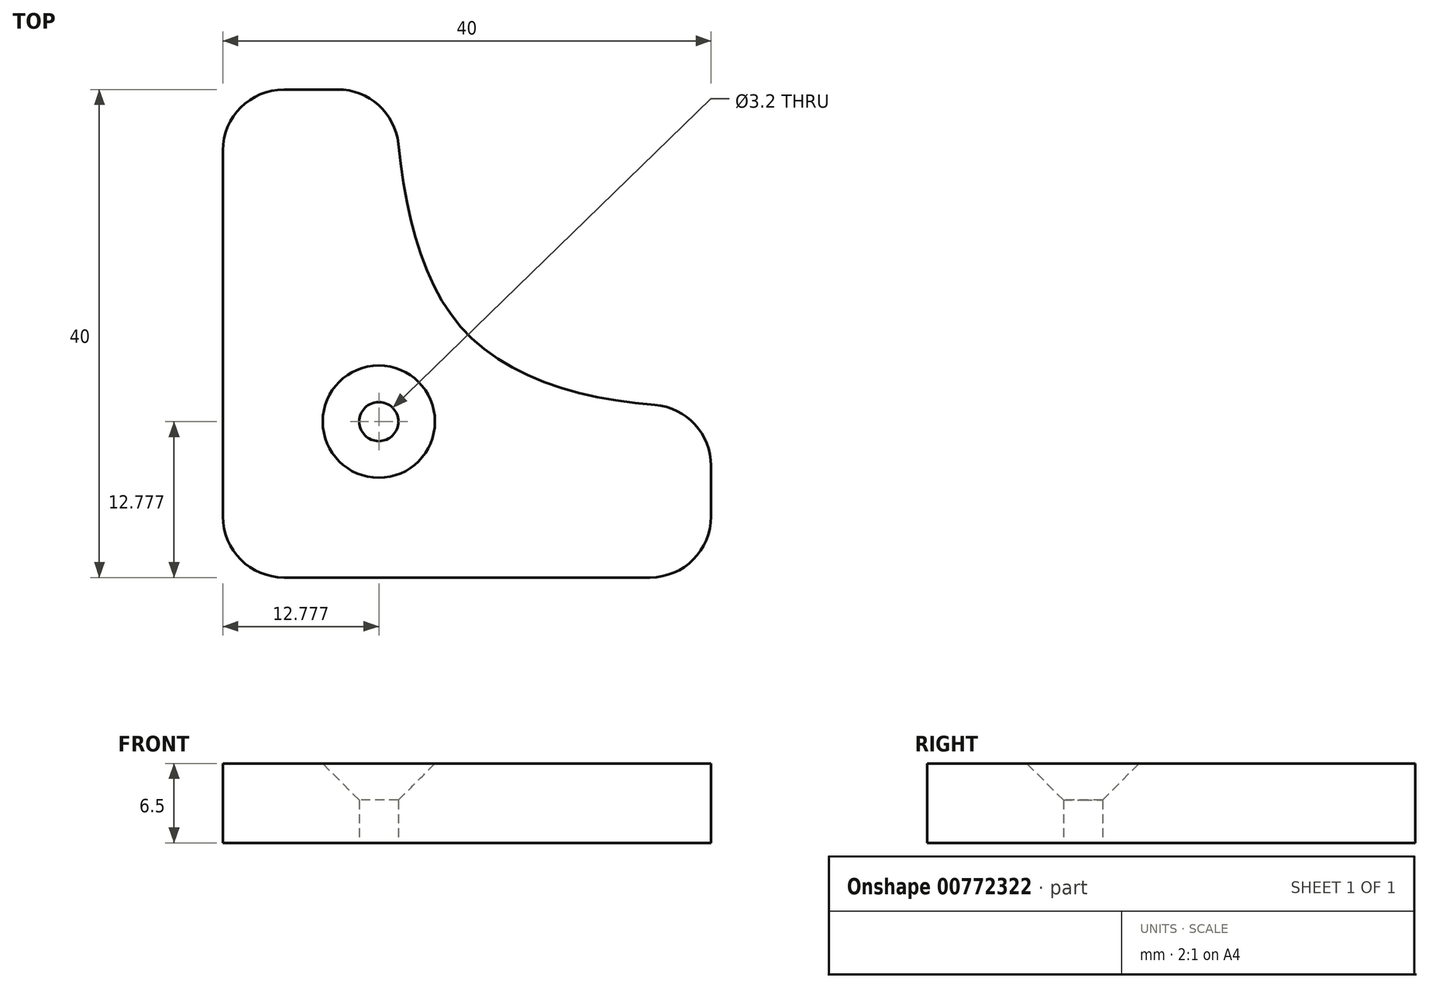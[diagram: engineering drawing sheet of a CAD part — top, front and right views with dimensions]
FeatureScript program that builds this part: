
annotation { "Feature Type Name" : "Feature", "Feature Type Description" : "" }
export const myFeature = defineFeature(function(context is Context, id is Id, definition is map)
    precondition{}
    {
        {
            assignVariable(context, id + "F0", {"name" : "h", "anyValue" : 6.5});
        }
        {
            var Q0;
            Q0=qCreatedBy(makeId("Top.planeOp"),FACE);
            var sketch = newSketch(context, id + "F1", { "sketchPlane" : qUnion([Q0])});
            skLineSegment(sketch, "E0.bottom", {"start": v(-20, 20) * mm, "end": v(20, 20) * mm});
            skLineSegment(sketch, "E0.top", {"start": v(-20, -20) * mm, "end": v(20, -20) * mm});
            skLineSegment(sketch, "E0.left", {"start": v(-20, 20) * mm, "end": v(-20, -20) * mm});
            skLineSegment(sketch, "E0.right", {"start": v(20, 20) * mm, "end": v(20, -20) * mm});
            skPoint(sketch, "E1", {"position": v(0, -20) * mm});
            skPoint(sketch, "E2", {"position": v(-20, 0) * mm});
            skFitSpline(sketch, "E3", {"points": [v(-6, 20) * mm, v(0, 0) * mm, v(20, -6) * mm], "startDerivative": vector(3.16, -47.96) * mm, "endDerivative": vector(47.54, 0.6) * mm});
            skLineSegment(sketch, "E4", {"start": v(-20, -20) * mm, "end": v(0, 0) * mm, "construction": true});
            skPoint(sketch, "E5", {"position": v(-7.22, -7.22) * mm});
            skCircle(sketch, "E6", {"center": v(-7.22, -7.22) * mm, "radius": 1.6 * mm});
            skSolve(sketch);
        }
        {
            var Q0;
            {var subQ1=sQuery(id+"F1.wireOp",EDGE,"E0.top");Q0=makeQuery(id+"F1.imprint","IMPRINT",FACE,{"disambiguationData":[TD([[makeQuery(id+"F1.imprint","IMPRINT",EDGE,{"derivedFrom":subQ1}),1.0]])]});}
            extrude(context, id + "F2", {"entities" : qUnion([Q0]), "depth" : (getVariable(context, 'h')) * mm, "offsetDistance" : 25 * mm});
        }
        {
            var Q0;
            Q0=makeQuery(id+"F2.opExtrude","CAP_EDGE",EDGE,{"disambiguationData":[OSD([sQuery(id+"F1.wireOp",EDGE,"E6")])],"isStart":false});
            chamfer(context, id + "F3", {"entities" : qUnion([Q0]), "width" : 3 * mm, "tangentPropagation" : true});
        }
        {
            var Q0;
            Q0=makeQuery(id+"F2.opExtrude","SWEPT_EDGE",EDGE,{"disambiguationData":[OSD([sQuery(id+"F1.wireOp",EDGE,"E0.top"),sQuery(id+"F1.wireOp",EDGE,"E0.left")])]});
            var Q1;
            Q1=makeQuery(id+"F2.opExtrude","SWEPT_EDGE",EDGE,{"disambiguationData":[OSD([sQuery(id+"F1.wireOp",EDGE,"E0.top"),sQuery(id+"F1.wireOp",EDGE,"E0.right")])]});
            var Q2;
            Q2=makeQuery(id+"F2.opExtrude","SWEPT_EDGE",EDGE,{"disambiguationData":[OSD([sQuery(id+"F1.wireOp",EDGE,"E0.right"),sQuery(id+"F1.wireOp",EDGE,"E3")])]});
            var Q3;
            Q3=makeQuery(id+"F2.opExtrude","SWEPT_EDGE",EDGE,{"disambiguationData":[OSD([sQuery(id+"F1.wireOp",EDGE,"E0.bottom"),sQuery(id+"F1.wireOp",EDGE,"E0.left")])]});
            var Q4;
            Q4=makeQuery(id+"F2.opExtrude","SWEPT_EDGE",EDGE,{"disambiguationData":[OSD([sQuery(id+"F1.wireOp",EDGE,"E0.bottom"),sQuery(id+"F1.wireOp",EDGE,"E3")])]});
            fillet(context, id + "F4", {"entities" : qUnion([Q0, Q1, Q2, Q3, Q4]), "radius" : 5 * mm, "tangentPropagation" : true, "allowEdgeOverflow" : false});
        }
    });
